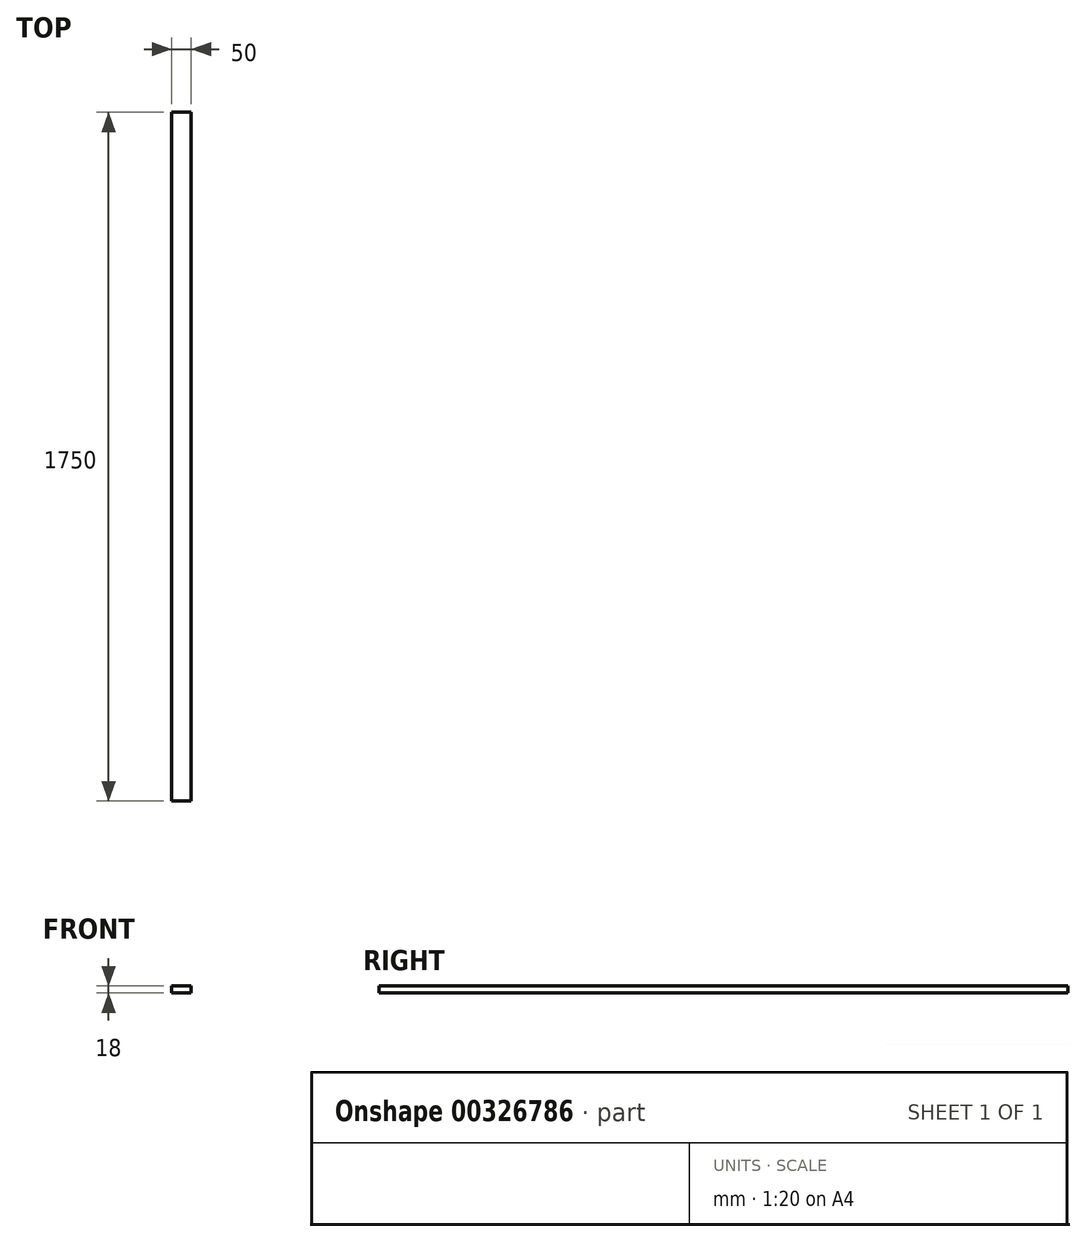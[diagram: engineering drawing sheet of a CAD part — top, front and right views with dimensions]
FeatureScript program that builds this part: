
annotation { "Feature Type Name" : "Feature", "Feature Type Description" : "" }
export const myFeature = defineFeature(function(context is Context, id is Id, definition is map)
    precondition{}
    {
        {
            var Q0;
            Q0=qCreatedBy(makeId("Top.planeOp"),FACE);
            var sketch = newSketch(context, id + "F0", { "sketchPlane" : qUnion([Q0])});
            skLineSegment(sketch, "E0.bottom", {"start": v(0, 0) * mm, "end": v(50, 0) * mm});
            skLineSegment(sketch, "E0.top", {"start": v(0, 1750) * mm, "end": v(50, 1750) * mm});
            skLineSegment(sketch, "E0.left", {"start": v(0, 0) * mm, "end": v(0, 1750) * mm});
            skLineSegment(sketch, "E0.right", {"start": v(50, 0) * mm, "end": v(50, 1750) * mm});
            skSolve(sketch);
        }
        {
            var Q0;
            Q0=qSketchRegion(id+"F0",true);
            extrude(context, id + "F1", {"entities" : qUnion([Q0]), "depth" : 18 * mm});
        }
    });
